# Revit family: NLRS_32_DO_Medinox_Helsinki
name_source: partatom
category: Doors
units: mm (PartAtom-declared; Revit-internal decimal feet)

## family parameters
Always vertical = Yes
Cut with Voids When Loaded = Yes
Host = Wall
OmniClass Number = 23.30.10.00
OmniClass Title = Doors
Room Calculation Point = No
Shared = Yes

## types (1)
- Medinox_2300x1000
    Analytic Construction = <None>
    Assembly Code = 32.32
    Comment = WHEN A DIFFERENT WINDOW SIZE IS REQUIRED, PLEASE CHECK WITH METAFLEX
    Height = 2268 mm  [stored 7.44094 ft]
    IFCExportAs = IfcDoorType
    IFCExportType = DOOR
    MFX_L_Canopy120 = 0 mm  [stored 0 ft]
    MFX_L_Centre_Height_Window = 1500 mm  [stored 4.92126 ft]
    MFX_L_FP = 800 mm  [stored 2.62467 ft]
    MFX_L_Height_Canopy = 2210 mm  [stored 7.25066 ft]
    MFX_L_Height_Cut-Out (Size Wall Opening) = 2311 mm
    MFX_L_Height_Handle = 1255 mm  [stored 4.11745 ft]
    MFX_L_IFH = 2200 mm
    MFX_L_IFH_1 = 2200 mm
    MFX_L_IFH_min max = 2268 mm  [stored 7.44094 ft]
    MFX_L_IFW = 920 mm
    MFX_L_IFW_Min_Max = 800 mm  [stored 2.62467 ft]
    MFX_L_Width_Cut-Out_Size Wall Opening = 1025 mm
    MFX_Motor_on_top and manual = Yes
    MFX_Opener_Var = 120 mm  [stored 0.393701 ft]
    MFX_Opener_Var_2 = 40 mm  [stored 0.131234 ft]
    MFX_YN_Canopy_BBU = Yes
    MFX_YN_Canopy_Ceiling = No
    MFX_YN_Canopy_High = No
    MFX_YN_Canopy_Low = No
    MFX_YN_Door = No
    MFX_YN_Door_With_Window = Yes
    MFX_YN_Door_With_Window_PB = No
    MFX_YN_Opener_Handle_Dgripp_Non_Track_Side = No
    MFX_YN_Opener_Handle_Dgripp_Track_Side = No
    MFX_YN_Opener_Handle_Dgripp_Track_Side_Recessed_Bowl_Non_Track_side = No
    MFX_YN_Opener_Hermetic_Lever = Yes
    MFX_YN_Opener_Recessed_Bowl_Non_Track_Side = No
    MFX_YN_Opener_Recessed_Bowl_Track_Side = No
    Manufacturer = Metaflex
    Model = Medinox
    Rough Height = 2243 mm  [stored 7.35892 ft]
    Rough Width = 0 mm  [stored 0 ft]
    Thickness = 0 mm  [stored 0 ft]
    Type Comments = Metaflex schuifdeur Medinox
    URL = www.metaflex.nl
    Wall Closure = By host
    Width = 800 mm  [stored 2.62467 ft]

note: [stored X ft] marks values corroborated as IEEE doubles in the binary element streams (Revit-internal decimal feet)

## geometry (parser evidence)
native form markers: Blend x12, Sweep x33
no freeform markers — native parametric forms only
